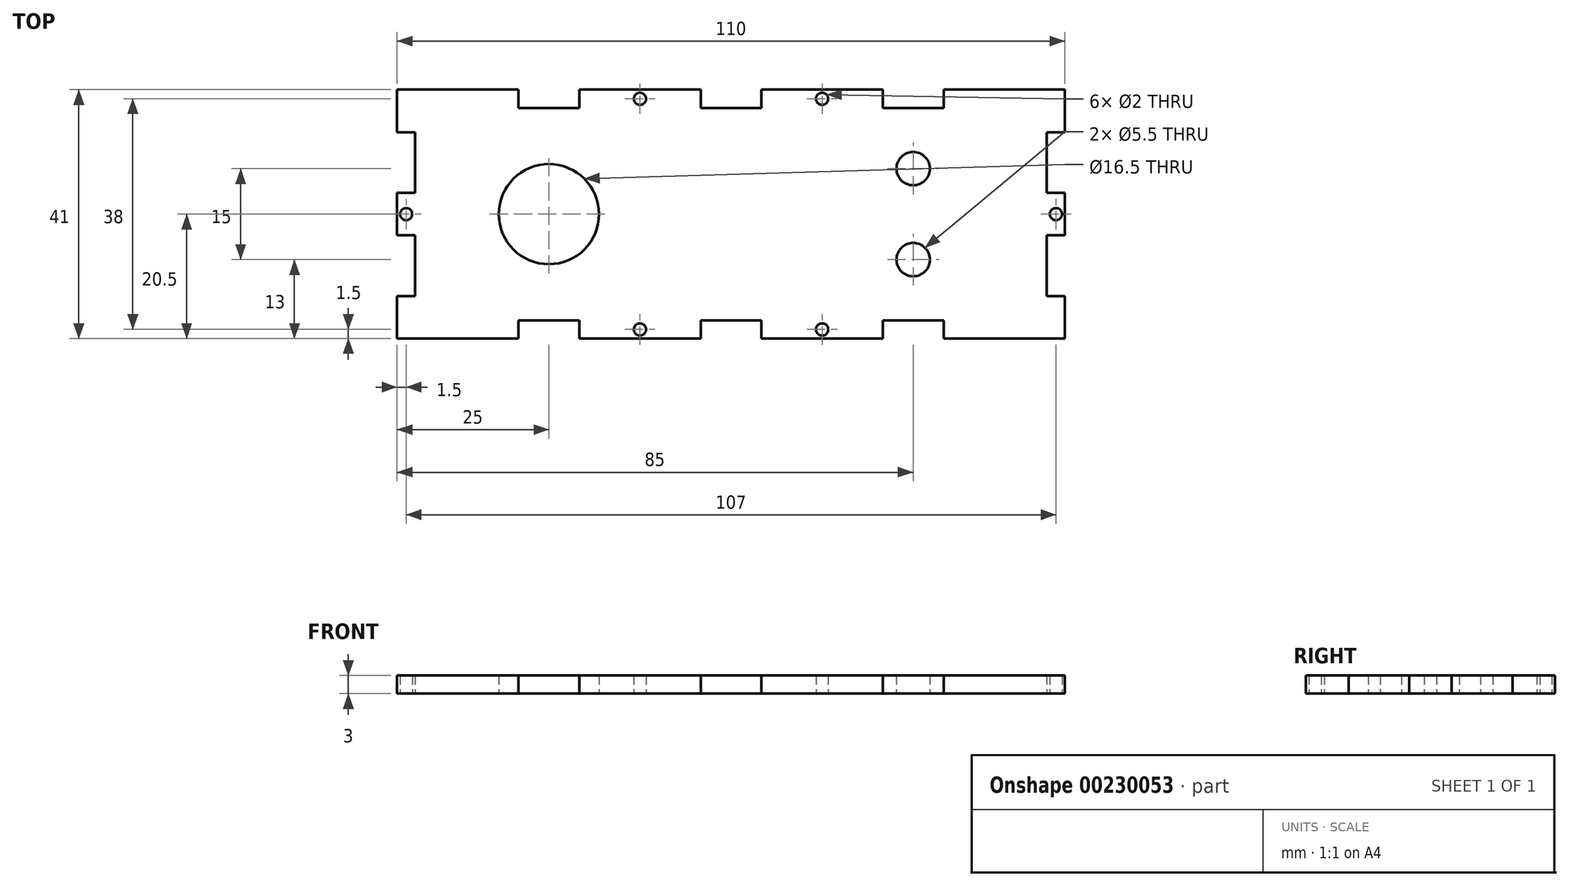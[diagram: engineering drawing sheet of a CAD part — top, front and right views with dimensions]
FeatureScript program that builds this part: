
annotation { "Feature Type Name" : "Feature", "Feature Type Description" : "" }
export const myFeature = defineFeature(function(context is Context, id is Id, definition is map)
    precondition{}
    {
        {
            var Q0;
            Q0=qCreatedBy(makeId("Top.planeOp"),FACE);
            var sketch = newSketch(context, id + "F0", { "sketchPlane" : qUnion([Q0])});
            skLineSegment(sketch, "E0", {"start": v(0, 0) * mm, "end": v(0, 7) * mm});
            skLineSegment(sketch, "E1", {"start": v(0, 7) * mm, "end": v(3, 7) * mm});
            skLineSegment(sketch, "E2", {"start": v(3, 7) * mm, "end": v(3, 17) * mm});
            skLineSegment(sketch, "E3", {"start": v(3, 17) * mm, "end": v(0, 17) * mm});
            skLineSegment(sketch, "E4", {"start": v(0, 17) * mm, "end": v(0, 24) * mm});
            skLineSegment(sketch, "E5", {"start": v(0, 24) * mm, "end": v(3, 24) * mm});
            skLineSegment(sketch, "E6", {"start": v(3, 34) * mm, "end": v(0, 34) * mm});
            skLineSegment(sketch, "E7", {"start": v(0, 34) * mm, "end": v(0, 41) * mm});
            skLineSegment(sketch, "E8", {"start": v(0, 41) * mm, "end": v(20, 41) * mm});
            skLineSegment(sketch, "E9", {"start": v(20, 41) * mm, "end": v(20, 38) * mm});
            skLineSegment(sketch, "E10", {"start": v(20, 38) * mm, "end": v(30, 38) * mm});
            skLineSegment(sketch, "E11", {"start": v(30, 38) * mm, "end": v(30, 41) * mm});
            skLineSegment(sketch, "E12", {"start": v(30, 41) * mm, "end": v(50, 41) * mm});
            skLineSegment(sketch, "E13", {"start": v(50, 41) * mm, "end": v(50, 38) * mm});
            skLineSegment(sketch, "E14", {"start": v(50, 38) * mm, "end": v(55, 38) * mm});
            skLineSegment(sketch, "E15", {"start": v(55, 38) * mm, "end": v(55, 3) * mm, "construction": true});
            skLineSegment(sketch, "E16", {"start": v(0, 0) * mm, "end": v(20, 0) * mm});
            skLineSegment(sketch, "E17", {"start": v(20, 0) * mm, "end": v(20, 3) * mm});
            skLineSegment(sketch, "E18", {"start": v(20, 3) * mm, "end": v(30, 3) * mm});
            skLineSegment(sketch, "E19", {"start": v(30, 3) * mm, "end": v(30, 0) * mm});
            skLineSegment(sketch, "E20", {"start": v(30, 0) * mm, "end": v(50, 0) * mm});
            skLineSegment(sketch, "E21", {"start": v(50, 0) * mm, "end": v(50, 3) * mm});
            skLineSegment(sketch, "E22", {"start": v(50, 3) * mm, "end": v(55, 3) * mm});
            skLineSegment(sketch, "E23.MirrorCS", {"start": v(80, 38) * mm, "end": v(80, 41) * mm});
            skLineSegment(sketch, "E24.MirrorCS", {"start": v(80, 3) * mm, "end": v(80, 0) * mm});
            skLineSegment(sketch, "E25.MirrorCS", {"start": v(90, 41) * mm, "end": v(90, 38) * mm});
            skLineSegment(sketch, "E26.MirrorCS", {"start": v(110, 24) * mm, "end": v(107, 24) * mm});
            skLineSegment(sketch, "E27.MirrorCS", {"start": v(90, 0) * mm, "end": v(90, 3) * mm});
            skLineSegment(sketch, "E28.MirrorCS", {"start": v(107, 34) * mm, "end": v(110, 34) * mm});
            skLineSegment(sketch, "E29.MirrorCS", {"start": v(110, 34) * mm, "end": v(110, 41) * mm});
            skLineSegment(sketch, "E30.MirrorCS", {"start": v(110, 17) * mm, "end": v(110, 24) * mm});
            skLineSegment(sketch, "E31.MirrorCS", {"start": v(60, 41) * mm, "end": v(60, 38) * mm});
            skLineSegment(sketch, "E32.MirrorCS", {"start": v(60, 38) * mm, "end": v(55, 38) * mm});
            skLineSegment(sketch, "E33.MirrorCS", {"start": v(107, 17) * mm, "end": v(110, 17) * mm});
            skLineSegment(sketch, "E34.MirrorCS", {"start": v(60, 0) * mm, "end": v(60, 3) * mm});
            skLineSegment(sketch, "E35.MirrorCS", {"start": v(110, 0) * mm, "end": v(110, 7) * mm});
            skLineSegment(sketch, "E36.MirrorCS", {"start": v(110, 7) * mm, "end": v(107, 7) * mm});
            skLineSegment(sketch, "E37.MirrorCS", {"start": v(60, 3) * mm, "end": v(55, 3) * mm});
            skLineSegment(sketch, "E38.MirrorCS", {"start": v(107, 7) * mm, "end": v(107, 17) * mm});
            skLineSegment(sketch, "E39.MirrorCS", {"start": v(90, 3) * mm, "end": v(80, 3) * mm});
            skLineSegment(sketch, "E40.MirrorCS", {"start": v(80, 0) * mm, "end": v(60, 0) * mm});
            skLineSegment(sketch, "E41.MirrorCS", {"start": v(107, 24) * mm, "end": v(107, 34) * mm});
            skLineSegment(sketch, "E42.MirrorCS", {"start": v(110, 41) * mm, "end": v(90, 41) * mm});
            skLineSegment(sketch, "E43.MirrorCS", {"start": v(110, 0) * mm, "end": v(90, 0) * mm});
            skLineSegment(sketch, "E44.MirrorCS", {"start": v(80, 41) * mm, "end": v(60, 41) * mm});
            skLineSegment(sketch, "E45.MirrorCS", {"start": v(90, 38) * mm, "end": v(80, 38) * mm});
            skPoint(sketch, "E46.centerSnap0", {"position": v(40, 41) * mm});
            skLineSegment(sketch, "E47", {"start": v(3, 34) * mm, "end": v(3, 24) * mm});
            skLineSegment(sketch, "E48.MirrorCS", {"start": v(55, 3) * mm, "end": v(55, 38) * mm, "construction": true});
            skCircle(sketch, "E49", {"center": v(1.5, 20.5) * mm, "radius": 1 * mm});
            skPoint(sketch, "E49.centerSnap0", {"position": v(1.5, 24) * mm});
            skPoint(sketch, "E49.centerSnap1", {"position": v(0, 20.5) * mm});
            skPoint(sketch, "E50.MirrorP", {"position": v(70, 41) * mm});
            skCircle(sketch, "E51.MirrorC", {"center": v(108.5, 20.5) * mm, "radius": 1 * mm});
            skPoint(sketch, "E52.MirrorP", {"position": v(110, 20.5) * mm});
            skPoint(sketch, "E53", {"position": v(70, 0) * mm});
            skCircle(sketch, "E54", {"center": v(40, 39.5) * mm, "radius": 1 * mm});
            skPoint(sketch, "E54.centerSnap0", {"position": v(50, 39.5) * mm});
            skCircle(sketch, "E55.MirrorC", {"center": v(40, 1.5) * mm, "radius": 1 * mm});
            skCircle(sketch, "E56.MirrorC", {"center": v(70, 1.5) * mm, "radius": 1 * mm});
            skCircle(sketch, "E57.MirrorC", {"center": v(70, 39.5) * mm, "radius": 1 * mm});
            skPoint(sketch, "E58.centerSnap0", {"position": v(85, 38) * mm});
            skCircle(sketch, "E59", {"center": v(25, 20.5) * mm, "radius": 8.25 * mm});
            skPoint(sketch, "E59.centerSnap0", {"position": v(25, 38) * mm});
            skCircle(sketch, "E60", {"center": v(85, 13) * mm, "radius": 2.75 * mm});
            skPoint(sketch, "E60.centerSnap0", {"position": v(85, 3) * mm});
            skCircle(sketch, "E61", {"center": v(85, 28) * mm, "radius": 2.75 * mm});
            skSolve(sketch);
        }
        {
            var Q0;
            Q0 = qSketchRegion(id + "F0", true);
            extrude(context, id + "F1", {"entities" : qUnion([Q0]), "depth" : 3 * mm});
        }
    });
